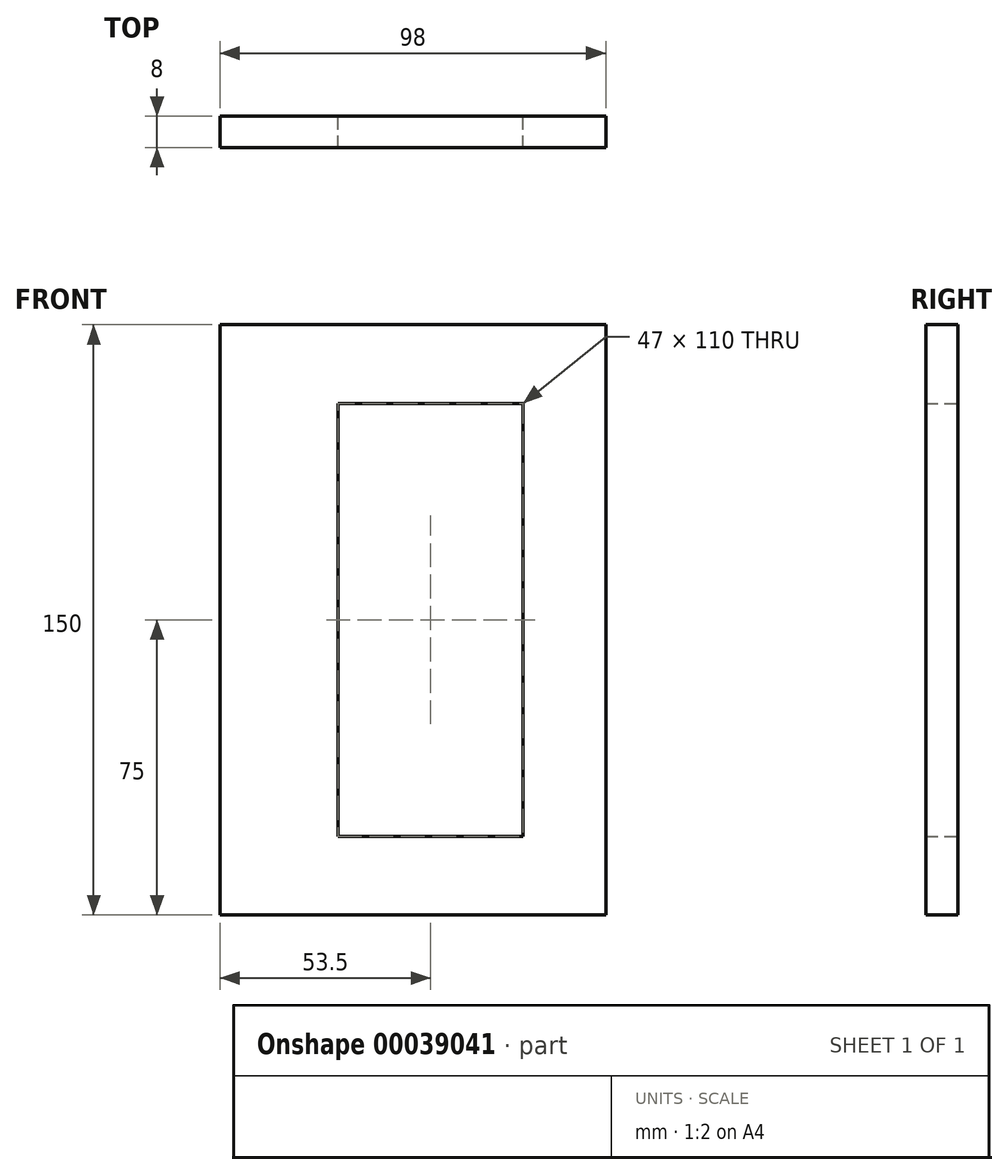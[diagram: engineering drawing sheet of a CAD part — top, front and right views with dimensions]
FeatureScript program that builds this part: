
annotation { "Feature Type Name" : "Feature", "Feature Type Description" : "" }
export const myFeature = defineFeature(function(context is Context, id is Id, definition is map)
    precondition{}
    {
        {
            var Q0;
            Q0=qCreatedBy(makeId("Front.planeOp"),FACE);
            var sketch = newSketch(context, id + "F0", { "sketchPlane" : qUnion([Q0])});
            skLineSegment(sketch, "E0.0", {"start": v(-40.5, -75) * mm, "end": v(57.5, -75) * mm});
            skLineSegment(sketch, "E1.0", {"start": v(57.5, 75) * mm, "end": v(57.5, -75) * mm});
            skLineSegment(sketch, "E2.0", {"start": v(-47.5, -75) * mm, "end": v(-47.5, 75) * mm, "construction": true});
            skLineSegment(sketch, "E3", {"start": v(-40.5, -75) * mm, "end": v(-40.5, 75) * mm});
            skLineSegment(sketch, "E4", {"start": v(-40.5, 75) * mm, "end": v(57.5, 75) * mm});
            skLineSegment(sketch, "E5.0", {"start": v(36.5, 55) * mm, "end": v(-10.5, 55) * mm});
            skLineSegment(sketch, "E6.0", {"start": v(-10.5, 55) * mm, "end": v(-10.5, -55) * mm});
            skLineSegment(sketch, "E7.0", {"start": v(-10.5, -55) * mm, "end": v(36.5, -55) * mm});
            skLineSegment(sketch, "E8", {"start": v(36.5, 55) * mm, "end": v(36.5, -55) * mm});
            skSolve(sketch);
        }
        {
            var Q0;
            Q0 = qSketchRegion(id + "F0", true);
            extrude(context, id + "F1", {"entities" : qUnion([Q0]), "depth" : 8 * mm});
        }
    });
